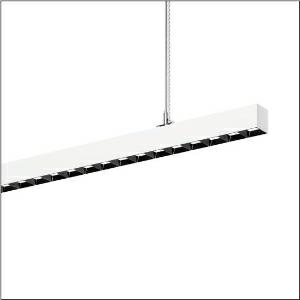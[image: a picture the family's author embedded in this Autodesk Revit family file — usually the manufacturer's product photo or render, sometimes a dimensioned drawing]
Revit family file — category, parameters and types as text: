
# Revit family: silica_21_51mx32dc3dwb
name_source: partatom
category: Lighting Fixtures
units: mm (PartAtom-declared; Revit-internal decimal feet)

## family parameters
Cut with Voids When Loaded = No
Host = Face
Light Source = No
Part Type = Normal
Room Calculation Point = No
Round Connector Dimension = Use Diameter
Shared = No

## types (1)
- --- (1 x LED, 18220 lm, 113 W, 3000K)
    Apparent Load = 113 VA
    CIE Flux Codes = 86 99 100 59 100
    Color Rendering = 80
    Color Temperature = 3000K
    Default Elevation = 1800 mm
    Description = Silica 21, office luminaire, primary light control with darklight reflector, of PMMA, black, CAT 2 (L<= 3000cd/m²), light emission: direct/indirect distribution, primary light characteristic: symmetric, installation type: suspended mounting, LED, rated luminous flux: 18.220lm, luminous efficacy: 161lm/W, light colour: 830, colour temperature: 3000K, control gear: DALI 2, with terminal, 3+2-pole, max. 2.5mm², mains connection: 220..240V, AC, 50/60Hz, rated input power: 113W, luminaire housing, of aluminium, traffic white (RAL 9016), length: 3.004mm, width: 53mm, height: 53mm, protection rating (complete): IP20, insulation class (complete): insulation class I (protective earthing), certification: CE, permissible operating ambient temperature: 0..+35°C, standard: EN 50419, packaging unit: 1 piece
    Height = 53 mm
    Lamp = 1 x LED
    Lamp Light Flux = 18220 lm
    Lamp Power = 113 W
    Lamp count = 1
    Length = 3004 mm
    Luminous efficacy = 161 lm/W
    Manufacturer = Siteco
    ModVariant = No
    Model = 51MX32DC3DWB
    Mounting Place = Ceiling
    Mounting Type = Pendant
    Number of Poles = 1
    OnlyDefault = Yes
    Power Factor = 1
    Product Name = Silica 21
    Product group = office luminaire | ceiling pendant
    ProductGroupID = 903
    Protection Class = Protection class I
    Protection Degree = IP 20
    RLX_Detail_Level = 1
    RLX_Emergency_Light_Flux = 0 lm
    RLX_Emergency_Type = 0
    RLX_Emergency_Type_DB = No
    RlxData = <blob elided: 65037 chars, md5=b7c94401>
    Socket = socket
    Standby Power = 0 W
    System Light Flux = 18220 lm
    System Power = 113 W
    Type Comments = factory setting: luminous flux: 100 % | dim-lin: 254 | 391 mA
    Type Image = l_1335871.jpg
    URL = http://relux.com
    VarID = @adj_122361
    Voltage = 0 V
    Weight = 0.00 kg
    Width = 53 mm

## geometry (parser evidence)
native form markers: Blend x4, Sweep x13
no freeform markers — native parametric forms only
